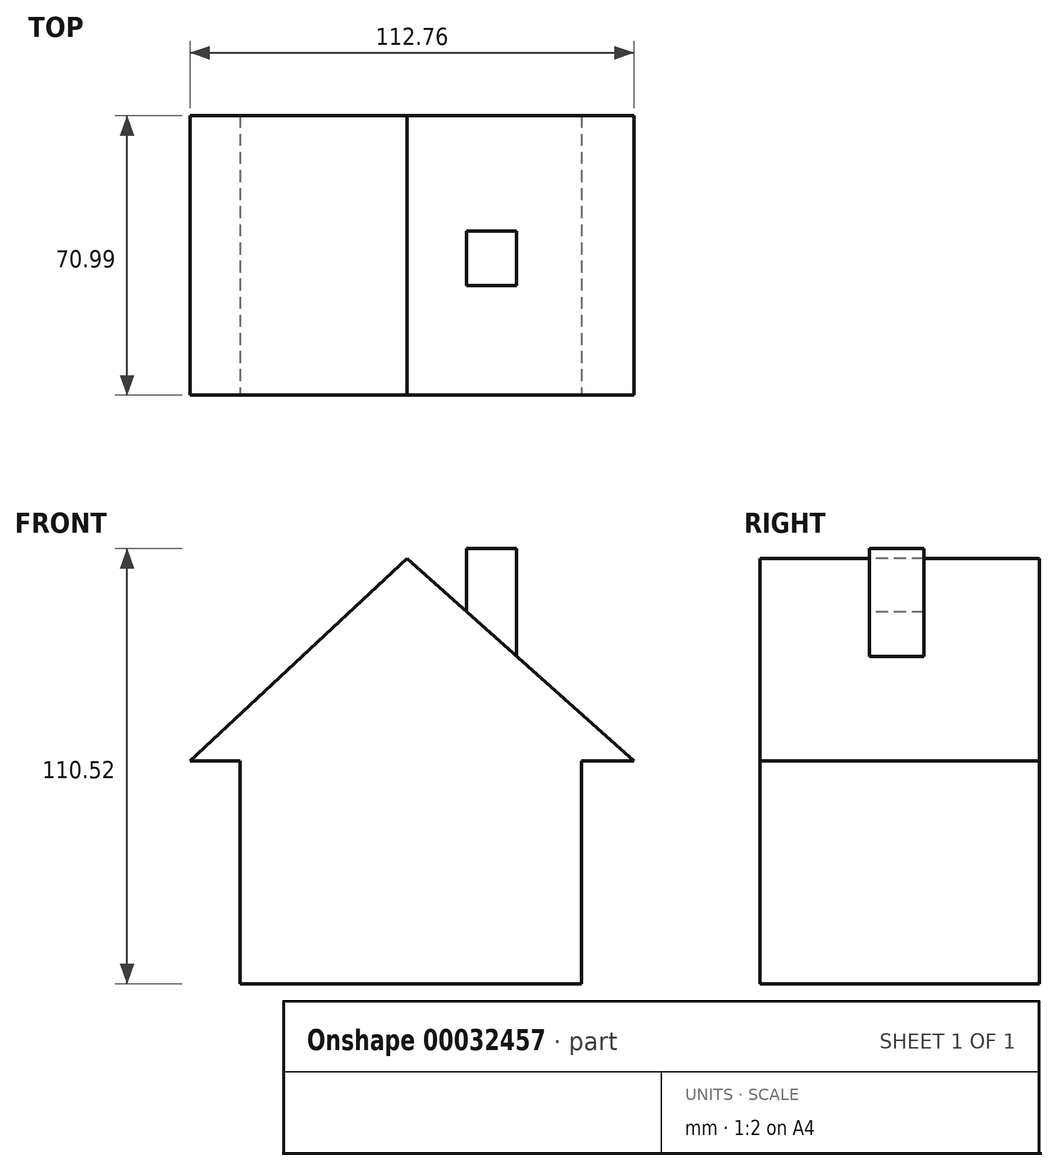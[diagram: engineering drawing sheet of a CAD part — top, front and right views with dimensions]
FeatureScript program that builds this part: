
annotation { "Feature Type Name" : "Feature", "Feature Type Description" : "" }
export const myFeature = defineFeature(function(context is Context, id is Id, definition is map)
    precondition{}
    {
        {
            var Q0;
            Q0=qCreatedBy(makeId("Front.planeOp"),FACE);
            var sketch = newSketch(context, id + "F0", { "sketchPlane" : qUnion([Q0])});
            skLineSegment(sketch, "E0", {"start": v(0, 51.35) * mm, "end": v(57.7, 0) * mm});
            skLineSegment(sketch, "E1", {"start": v(0, 51.35) * mm, "end": v(-55.05, 0) * mm});
            skLineSegment(sketch, "E2", {"start": v(-42.33, 0) * mm, "end": v(44.42, 0) * mm});
            skLineSegment(sketch, "E3", {"start": v(-42.33, 0) * mm, "end": v(-42.33, -56.66) * mm});
            skLineSegment(sketch, "E4", {"start": v(44.42, 0) * mm, "end": v(44.42, -56.66) * mm});
            skLineSegment(sketch, "E5", {"start": v(-42.33, -56.66) * mm, "end": v(44.42, -56.66) * mm});
            skLineSegment(sketch, "E6", {"start": v(-55.05, 0) * mm, "end": v(-42.33, 0) * mm});
            skLineSegment(sketch, "E7", {"start": v(57.7, 0) * mm, "end": v(44.42, 0) * mm});
            skLineSegment(sketch, "E8", {"start": v(-55.05, 0) * mm, "end": v(57.7, 0) * mm});
            skSolve(sketch);
        }
        {
            var Q0;
            {var subQ2=sQuery(id+"F0.wireOp",EDGE,"E3");Q0=makeQuery(id+"F0.imprint","IMPRINT",FACE,{"disambiguationData":[TD([[makeQuery(id+"F0.imprint","IMPRINT",EDGE,{"derivedFrom":subQ2}),1.0]])]});}
            var Q1;
            {var subQ4=sQuery(id+"F0.wireOp",EDGE,"E0");Q1=makeQuery(id+"F0.imprint","IMPRINT",FACE,{"disambiguationData":[TD([[makeQuery(id+"F0.imprint","IMPRINT",EDGE,{"derivedFrom":subQ4}),-1.0]])]});}
            extrude(context, id + "F1", {"entities" : qUnion([Q0, Q1]), "oppositeDirection" : true, "depth" : 71 * mm});
        }
        {
            var Q0;
            Q0=qCreatedBy(makeId("Top.planeOp"),FACE);
            var sketch = newSketch(context, id + "F2", { "sketchPlane" : qUnion([Q0])});
            skLineSegment(sketch, "E9.bottom", {"start": v(15.19, 41.67) * mm, "end": v(27.9, 41.67) * mm});
            skLineSegment(sketch, "E9.top", {"start": v(15.19, 27.8) * mm, "end": v(27.9, 27.8) * mm});
            skLineSegment(sketch, "E9.left", {"start": v(15.19, 41.67) * mm, "end": v(15.19, 27.8) * mm});
            skLineSegment(sketch, "E9.right", {"start": v(27.9, 41.67) * mm, "end": v(27.9, 27.8) * mm});
            skSolve(sketch);
        }
        {
            var Q0;
            Q0 = qSketchRegion(id + "F2", true);
            extrude(context, id + "F3", {"entities" : qUnion([Q0]), "operationType" : NewBodyOperationType.ADD, "depth" : 53.86 * mm});
        }
    });
